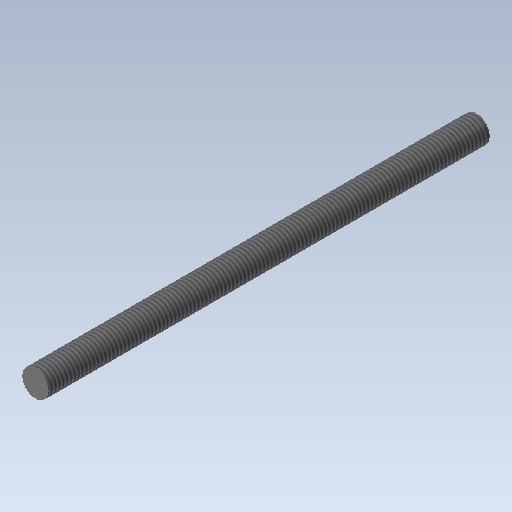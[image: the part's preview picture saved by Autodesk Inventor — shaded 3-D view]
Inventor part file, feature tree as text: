
AUTODESK INVENTOR PART (.ipt)
format: ipt  version: 2021.3 (Build 253353000, 353)  size: 124,928 bytes
history: native  units: mm
features: extrude x1, thread x1, sketch x1
ambient origin geometry x8: Origin, YZ Plane, XZ Plane, XY Plane, X Axis, Y Axis, Z Axis, Center Point
bodies: Solid1 (feature_tree)
feature tree (3):
  extrude  "Extrusion1"  Depth=200.0mm TaperAngle=0.0deg
  thread  "Thread2"  [1 undecoded]
  sketch  "Sketch1"  dims[d0=12.0mm d1=200.0mm d2=0.0mm d5=10.0mm d6=0.0mm]
note: 1 required parameter value undecoded (feature->parameter linkage not recoverable at this tier; creation-order binding heuristic only, values carry confidence <= 0.55)
